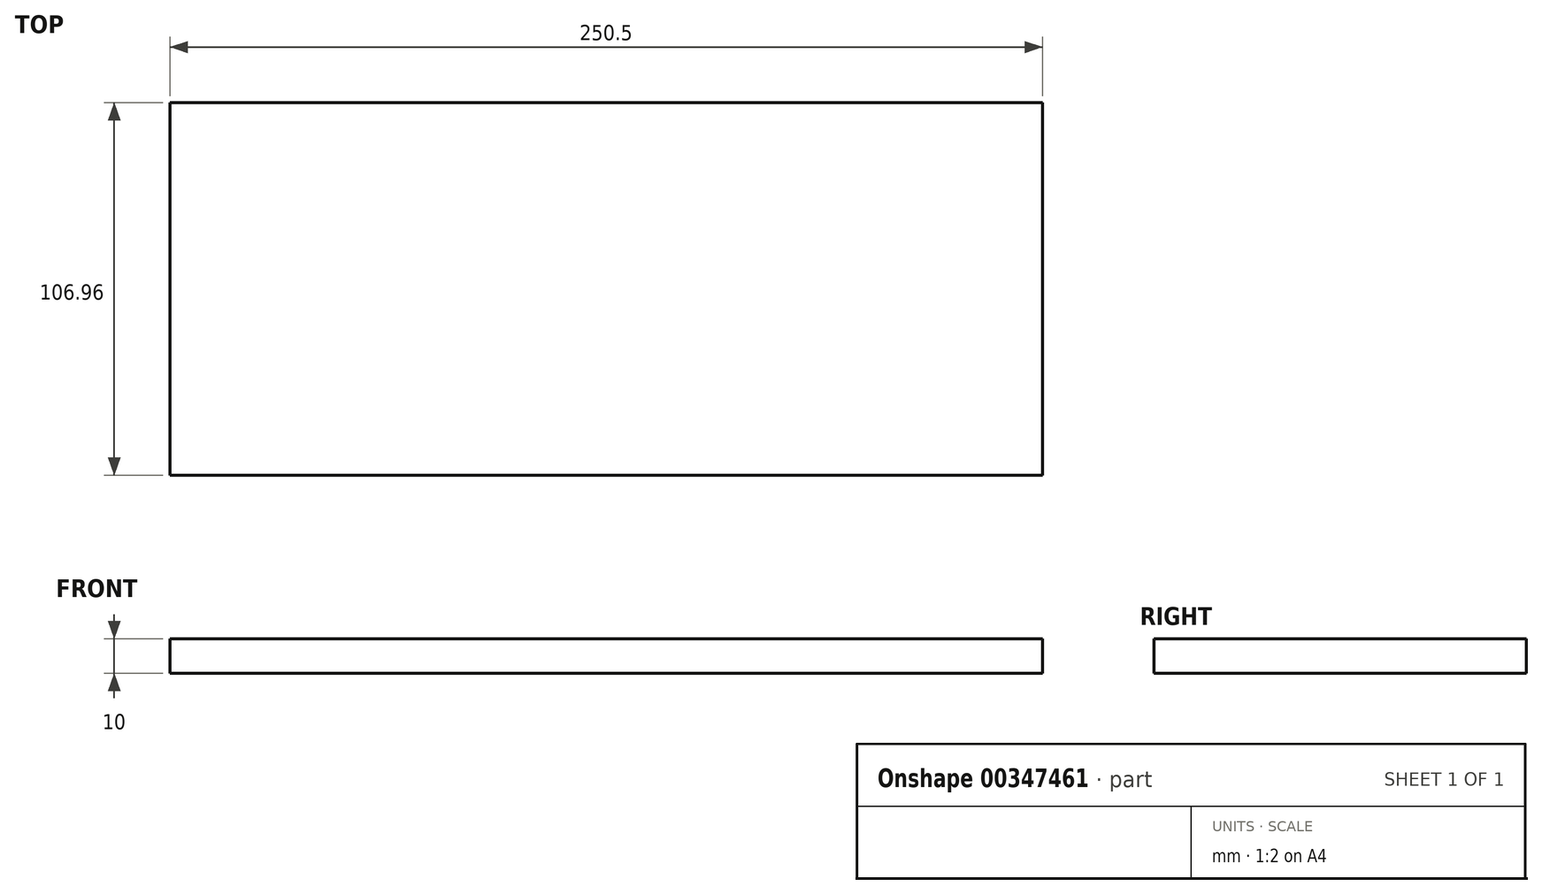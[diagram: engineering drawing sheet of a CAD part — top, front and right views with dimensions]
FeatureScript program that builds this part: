
annotation { "Feature Type Name" : "Feature", "Feature Type Description" : "" }
export const myFeature = defineFeature(function(context is Context, id is Id, definition is map)
    precondition{}
    {
        {
            var Q0;
            Q0=qCreatedBy(makeId("Top.planeOp"),FACE);
            var sketch = newSketch(context, id + "F0", { "sketchPlane" : qUnion([Q0])});
            skLineSegment(sketch, "E0.bottom", {"start": v(125.25, -53.48) * mm, "end": v(-125.25, -53.48) * mm});
            skLineSegment(sketch, "E0.top", {"start": v(125.25, 53.48) * mm, "end": v(-125.25, 53.48) * mm});
            skLineSegment(sketch, "E0.left", {"start": v(125.25, -53.48) * mm, "end": v(125.25, 53.48) * mm});
            skLineSegment(sketch, "E0.right", {"start": v(-125.25, -53.48) * mm, "end": v(-125.25, 53.48) * mm});
            skPoint(sketch, "E0.middle", {"position": v(0, 0) * mm});
            skSolve(sketch);
        }
        {
            var Q0;
            Q0=makeQuery(id+"F0.imprint","IMPRINT",FACE,{"disambiguationData":[TD([[makeQuery(id+"F0.imprint","IMPRINT",EDGE,{"derivedFrom":sQuery(id+"F0.wireOp",EDGE,"E0.bottom")}),-1.0]])]});
            extrude(context, id + "F1", {"entities" : qUnion([Q0]), "oppositeDirection" : true, "depth" : 10 * mm});
        }
    });
